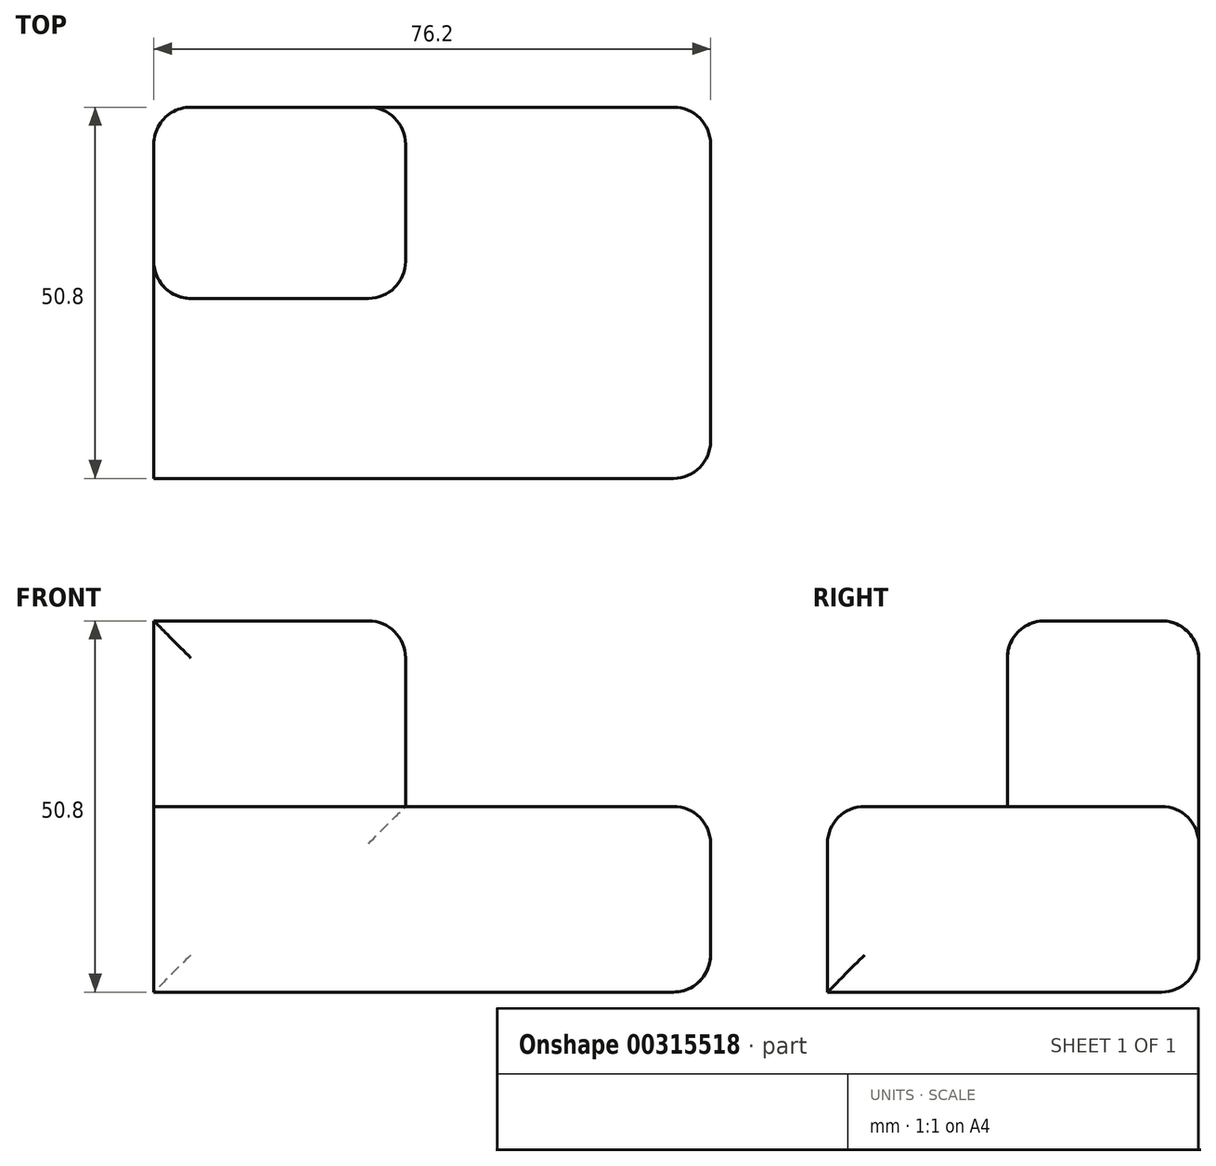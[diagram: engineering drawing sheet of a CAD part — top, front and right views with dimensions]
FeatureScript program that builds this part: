
annotation { "Feature Type Name" : "Feature", "Feature Type Description" : "" }
export const myFeature = defineFeature(function(context is Context, id is Id, definition is map)
    precondition{}
    {
        {
            var Q0;
            Q0=qCreatedBy(makeId("Top.planeOp"),FACE);
            var sketch = newSketch(context, id + "F0", { "sketchPlane" : qUnion([Q0])});
            skLineSegment(sketch, "E0.bottom", {"start": v(-23.93, 26.18) * mm, "end": v(52.27, 26.18) * mm});
            skLineSegment(sketch, "E0.top", {"start": v(-23.93, -24.62) * mm, "end": v(52.27, -24.62) * mm});
            skLineSegment(sketch, "E0.left", {"start": v(-23.93, 26.18) * mm, "end": v(-23.93, -24.62) * mm});
            skLineSegment(sketch, "E0.right", {"start": v(52.27, 26.18) * mm, "end": v(52.27, -24.62) * mm});
            skSolve(sketch);
        }
        {
            var Q0;
            Q0 = qSketchRegion(id + "F0", true);
            extrude(context, id + "F1", {"entities" : qUnion([Q0]), "depth" : 25.4 * mm});
        }
        {
            var Q0;
            Q0=makeQuery(id+"F1.opExtrude","CAP_FACE",FACE,{"disambiguationData":[OSD([sQuery(id+"F0.wireOp",EDGE,"E0.bottom"),sQuery(id+"F0.wireOp",EDGE,"E0.top"),sQuery(id+"F0.wireOp",EDGE,"E0.left"),sQuery(id+"F0.wireOp",EDGE,"E0.right")])],"isStart":false});
            var sketch = newSketch(context, id + "F2", { "sketchPlane" : qUnion([Q0])});
            skLineSegment(sketch, "E1.bottom", {"start": v(-23.93, 26.18) * mm, "end": v(10.53, 26.18) * mm});
            skLineSegment(sketch, "E1.top", {"start": v(-23.93, 0) * mm, "end": v(10.53, 0) * mm});
            skLineSegment(sketch, "E1.left", {"start": v(-23.93, 26.18) * mm, "end": v(-23.93, 0) * mm});
            skLineSegment(sketch, "E1.right", {"start": v(10.53, 26.18) * mm, "end": v(10.53, 0) * mm});
            skSolve(sketch);
        }
        {
            var Q0;
            Q0=makeQuery(id+"F2.imprint","IMPRINT",FACE,{"disambiguationData":[TD([[makeQuery(id+"F2.imprint","IMPRINT",EDGE,{"derivedFrom":sQuery(id+"F2.wireOp",EDGE,"E1.bottom")}),-1.0]])]});
            extrude(context, id + "F3", {"entities" : qUnion([Q0]), "operationType" : NewBodyOperationType.ADD, "depth" : 25.4 * mm});
        }
        {
            var Q0;
            Q0=makeQuery(id+"F3.opExtrude","CAP_EDGE",EDGE,{"disambiguationData":[OSD([sQuery(id+"F2.wireOp",EDGE,"E1.top")])],"isStart":true});
            var Q1;
            Q1=makeQuery(id+"F3.opExtrude","CAP_EDGE",EDGE,{"disambiguationData":[OSD([sQuery(id+"F2.wireOp",EDGE,"E1.right")])],"isStart":true});
            var Q2;
            Q2=makeQuery(id+"F1.opExtrude","CAP_EDGE",EDGE,{"disambiguationData":[OSD([sQuery(id+"F0.wireOp",EDGE,"E0.top")])],"isStart":false});
            var Q3;
            Q3=makeQuery(id+"F1.opExtrude","CAP_EDGE",EDGE,{"disambiguationData":[OSD([sQuery(id+"F0.wireOp",EDGE,"E0.right")])],"isStart":false});
            var Q4;
            Q4=makeQuery(id+"F1.opExtrude","SWEPT_EDGE",EDGE,{"disambiguationData":[OSD([sQuery(id+"F0.wireOp",EDGE,"E0.top"),sQuery(id+"F0.wireOp",EDGE,"E0.right")])]});
            var Q5;
            Q5=makeQuery(id+"F1.opExtrude","SWEPT_EDGE",EDGE,{"disambiguationData":[OSD([sQuery(id+"F0.wireOp",EDGE,"E0.bottom"),sQuery(id+"F0.wireOp",EDGE,"E0.right")])]});
            var Q6;
            Q6=makeQuery(id+"F1.opExtrude","CAP_EDGE",EDGE,{"disambiguationData":[OSD([sQuery(id+"F0.wireOp",EDGE,"E0.right")])],"isStart":true});
            var Q7;
            Q7=makeQuery(id+"F1.opExtrude","CAP_EDGE",EDGE,{"disambiguationData":[OSD([sQuery(id+"F0.wireOp",EDGE,"E0.bottom")])],"isStart":true});
            var Q8;
            Q8=makeQuery(id+"F1.opExtrude","CAP_EDGE",EDGE,{"disambiguationData":[OSD([sQuery(id+"F0.wireOp",EDGE,"E0.bottom")])],"isStart":false});
            var Q9;
            Q9=makeQuery(id+"F3.opExtrude","CAP_EDGE",EDGE,{"disambiguationData":[OSD([sQuery(id+"F2.wireOp",EDGE,"E1.bottom")])],"isStart":false});
            var Q10;
            Q10=makeQuery(id+"F3.boolean.opBoolean","MERGE",EDGE,{"derivedFrom":[makeQuery(id+"F1.opExtrude","SWEPT_EDGE",EDGE,{"disambiguationData":[OSD([sQuery(id+"F0.wireOp",EDGE,"E0.bottom"),sQuery(id+"F0.wireOp",EDGE,"E0.left")])]}),makeQuery(id+"F3.opExtrude","SWEPT_EDGE",EDGE,{"disambiguationData":[OSD([sQuery(id+"F2.wireOp",EDGE,"E1.bottom"),sQuery(id+"F2.wireOp",EDGE,"E1.left")])]})]});
            var Q11;
            Q11=makeQuery(id+"F3.opExtrude","CAP_EDGE",EDGE,{"disambiguationData":[OSD([sQuery(id+"F2.wireOp",EDGE,"E1.right")])],"isStart":false});
            var Q12;
            Q12=makeQuery(id+"F3.opExtrude","CAP_EDGE",EDGE,{"disambiguationData":[OSD([sQuery(id+"F2.wireOp",EDGE,"E1.top")])],"isStart":false});
            var Q13;
            Q13=makeQuery(id+"F3.opExtrude","SWEPT_EDGE",EDGE,{"disambiguationData":[OSD([sQuery(id+"F0.wireOp",EDGE,"E0.left"),sQuery(id+"F2.wireOp",EDGE,"E1.top"),sQuery(id+"F2.wireOp",EDGE,"E1.left")])]});
            var Q14;
            Q14=makeQuery(id+"F3.opExtrude","SWEPT_EDGE",EDGE,{"disambiguationData":[OSD([sQuery(id+"F2.wireOp",EDGE,"E1.top"),sQuery(id+"F2.wireOp",EDGE,"E1.right")])]});
            var Q15;
            Q15=makeQuery(id+"F3.opExtrude","SWEPT_EDGE",EDGE,{"disambiguationData":[OSD([sQuery(id+"F0.wireOp",EDGE,"E0.bottom"),sQuery(id+"F2.wireOp",EDGE,"E1.bottom"),sQuery(id+"F2.wireOp",EDGE,"E1.right")])]});
            fillet(context, id + "F4", {"entities" : qUnion([Q0, Q1, Q2, Q3, Q4, Q5, Q6, Q7, Q8, Q9, Q10, Q11, Q12, Q13, Q14, Q15]), "radius" : 5.08 * mm, "tangentPropagation" : true, "allowEdgeOverflow" : false});
        }
    });
